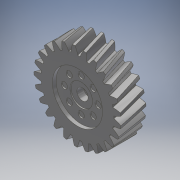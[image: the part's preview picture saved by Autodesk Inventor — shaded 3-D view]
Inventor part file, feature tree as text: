
AUTODESK INVENTOR PART (.ipt)
format: ipt  version: 2019 (Build 230136000, 136)  size: 583,168 bytes
history: native  units: mm (DEFAULTED — no unit token found)
features: sketch x10, extrude x7, plane x3, other x3, hole x2, chamfer x1
ambient origin geometry x8: Origin, YZ Plane, XZ Plane, XY Plane, X Axis, Y Axis, Z Axis, Center Point
bodies: Solid1 (feature_tree)
feature tree (26):
  extrude  "Extrusion1"  Depth=10.0mm TaperAngle=0.0deg
  plane  "Work Plane2"
  plane  "Work Plane8"
  plane  "Work Plane9"
  other  "Spur Gear"
  hole  "Hole1"  [1 undecoded]
  extrude  "Extrusion4"  Depth=1.256637mm TaperAngle=0.0deg
  extrude  "Extrusion6"  TaperAngle=0.0deg  [1 undecoded]
  hole  "Hole3"  [1 undecoded]
  extrude  "Extrusion8"  Depth=8.0mm
  chamfer  "Chamfer1"  Distance=1.5mm
  extrude  "Extrusion9"  Depth=9.0mm
  extrude  "Extrusion10"  Depth=5.0mm
  extrude  "Extrusion12"  Depth=5.0mm TaperAngle=0.0deg
  sketch  "Sketch1"  dims[d0=34.756617mm d1=10.0mm d2=0.0mm]
  sketch  "Sketch2"  dims[d3=32.258065mm d4=10.0mm d5=0.0mm]
  other  "Srf1"
  sketch  "Sketch5"  dims[d16=40.0mm d17=0.0mm d34=1.256637mm]
  sketch  "Sketch6"  dims[d39=0.0mm d41=0.0mm]
  sketch  "Sketch10"  dims[d43=40.0mm d46=40.0mm]
  sketch  "Sketch11"  dims[d47=0.0mm d48=0.0mm]
  sketch  "Sketch14"  dims[d55=4.5mm d56=6.0mm d57=6.5mm d58=4.0mm d59=90.0deg d60=8.0mm d61=20.594885mm d62=20.0mm d63=1.5mm d64=0.0mm]
  sketch  "Sketch15"  dims[d82=18.0mm d83=9.0mm]
  sketch  "Sketch16"  dims[d84=5.0mm d85=0.0mm d86=13.5mm]
  sketch  "Sketch18"  dims[d87=80.0mm d89=360.0deg d91=2.5mm d92=6.0mm d93=4.0mm d94=3.0mm d95=90.0deg d96=8.0mm d97=20.594885mm d100=5.0mm d101=0.0mm d102=1.5mm d103=4.0mm d104=12.217305mm d105=9.0mm d106=0.5mm d107=0.0mm d108=80.0mm d110=360.0deg d112=0.3mm d113=0.0mm d120=80.0mm d122=360.0deg d124=0.3mm d125=0.0mm]
  other  "Pitch Diameter"
note: 3 required parameter values undecoded (feature->parameter linkage not recoverable at this tier; creation-order binding heuristic only, values carry confidence <= 0.55)
